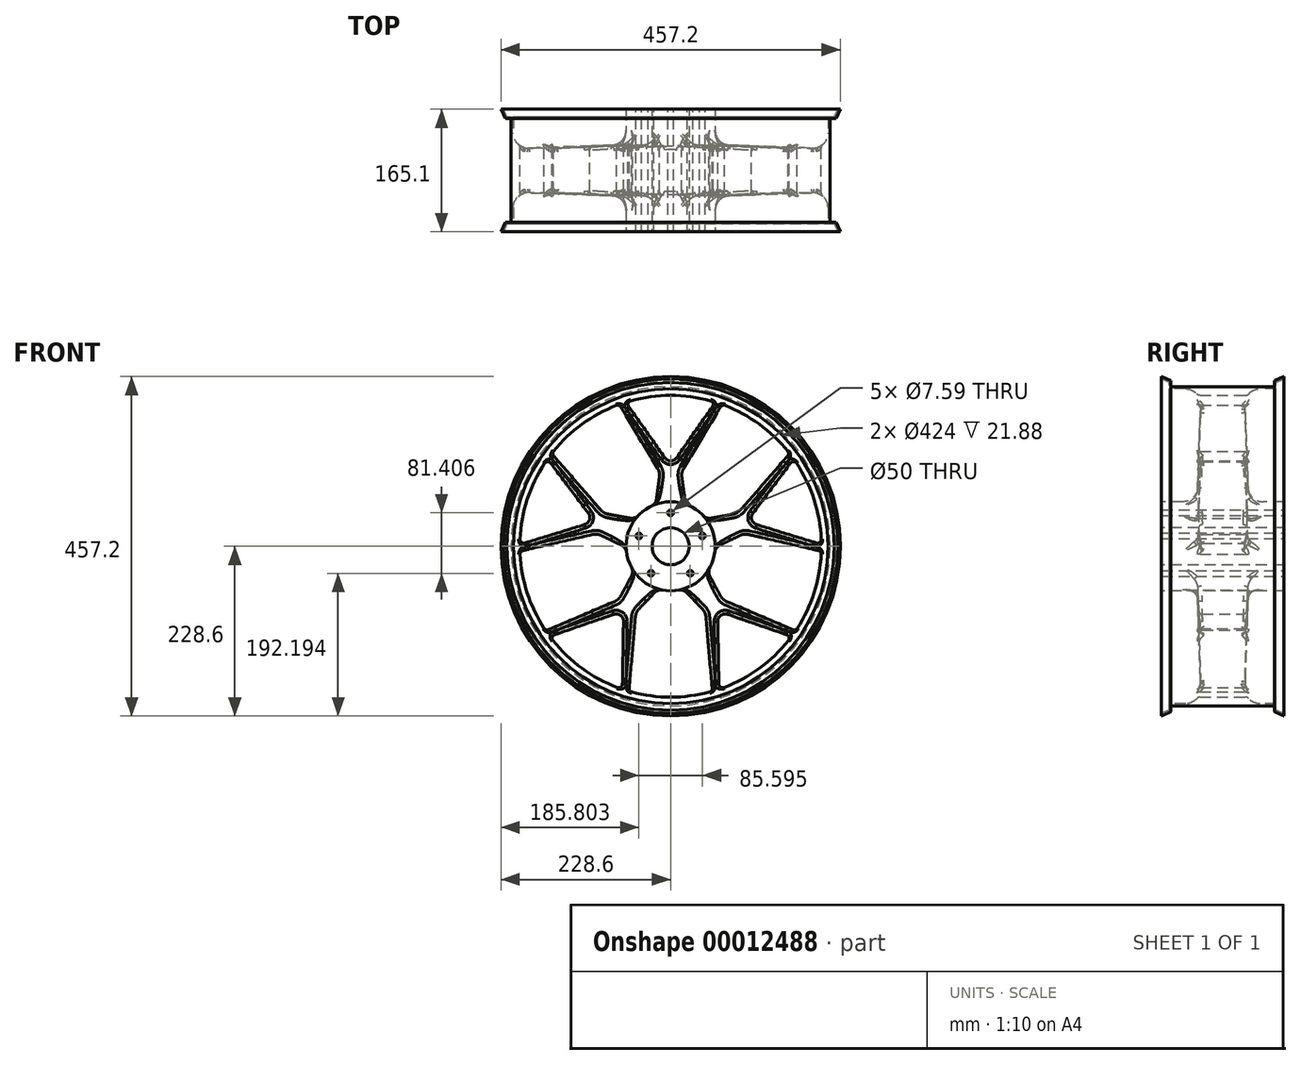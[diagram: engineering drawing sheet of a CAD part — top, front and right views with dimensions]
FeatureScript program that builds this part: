
annotation { "Feature Type Name" : "Feature", "Feature Type Description" : "" }
export const myFeature = defineFeature(function(context is Context, id is Id, definition is map)
    precondition{}
    {
        {
            var Q0;
            Q0=qCreatedBy(makeId("Right.planeOp"),FACE);
            var sketch = newSketch(context, id + "F0", { "sketchPlane" : qUnion([Q0])});
            skLineSegment(sketch, "E0", {"start": v(0, 0) * mm, "end": v(0, 215) * mm, "construction": true});
            skLineSegment(sketch, "E1", {"start": v(0, 215) * mm, "end": v(69.85, 215) * mm});
            skLineSegment(sketch, "E2", {"start": v(69.85, 215) * mm, "end": v(69.85, 223) * mm});
            skLineSegment(sketch, "E3", {"start": v(69.85, 223) * mm, "end": v(82.55, 228.6) * mm});
            skLineSegment(sketch, "E4", {"start": v(82.55, 228.6) * mm, "end": v(82.55, 225.32) * mm});
            skLineSegment(sketch, "E5", {"start": v(82.55, 225.32) * mm, "end": v(71.85, 220.6) * mm});
            skLineSegment(sketch, "E6", {"start": v(71.85, 220.6) * mm, "end": v(71.85, 212) * mm});
            skLineSegment(sketch, "E7", {"start": v(71.85, 212) * mm, "end": v(49.97, 212) * mm});
            skLineSegment(sketch, "E8", {"start": v(0, 0) * mm, "end": v(213.47, 0) * mm, "construction": true});
            skLineSegment(sketch, "E9", {"start": v(53.9, 60) * mm, "end": v(82.55, 60) * mm});
            skLineSegment(sketch, "E10", {"start": v(82.55, 60) * mm, "end": v(82.55, 25) * mm});
            skLineSegment(sketch, "E11", {"start": v(82.55, 25) * mm, "end": v(0, 25) * mm});
            skArc(sketch, "E12.filletArc", {"start": v(49.97, 212) * mm, "mid": v(35.6, 205.9) * mm, "end": v(30, 191.32) * mm});
            skLineSegment(sketch, "E13", {"start": v(30, 191.32) * mm, "end": v(33.91, 79.3) * mm});
            skPoint(sketch, "E14.newPointB", {"position": v(0, 60) * mm});
            skPoint(sketch, "E15.visualSharp", {"position": v(34.59, 60) * mm});
            skArc(sketch, "E15.filletArc", {"start": v(33.91, 79.3) * mm, "mid": v(40, 65.61) * mm, "end": v(53.9, 60) * mm});
            skLineSegment(sketch, "E16.0.MirrorCS", {"start": v(-69.85, 215) * mm, "end": v(-69.85, 223) * mm});
            skLineSegment(sketch, "E16.1.MirrorCS", {"start": v(-82.55, 228.6) * mm, "end": v(-82.55, 225.32) * mm});
            skLineSegment(sketch, "E16.2.MirrorCS", {"start": v(-71.85, 220.6) * mm, "end": v(-71.85, 212) * mm});
            skLineSegment(sketch, "E16.3.MirrorCS", {"start": v(-82.55, 225.32) * mm, "end": v(-71.85, 220.6) * mm});
            skLineSegment(sketch, "E16.4.MirrorCS", {"start": v(-82.55, 25) * mm, "end": v(0, 25) * mm});
            skArc(sketch, "E16.5.MirrorCS", {"start": v(-49.97, 212) * mm, "mid": v(-35.6, 205.9) * mm, "end": v(-30, 191.32) * mm});
            skLineSegment(sketch, "E16.6.MirrorCS", {"start": v(-53.9, 60) * mm, "end": v(-82.55, 60) * mm});
            skPoint(sketch, "E16.7.MirrorP", {"position": v(-34.59, 60) * mm});
            skLineSegment(sketch, "E16.8.MirrorCS", {"start": v(-69.85, 223) * mm, "end": v(-82.55, 228.6) * mm});
            skLineSegment(sketch, "E16.9.MirrorCS", {"start": v(-82.55, 60) * mm, "end": v(-82.55, 25) * mm});
            skLineSegment(sketch, "E16.10.MirrorCS", {"start": v(-71.85, 212) * mm, "end": v(-49.97, 212) * mm});
            skLineSegment(sketch, "E16.11.MirrorCS", {"start": v(0, 215) * mm, "end": v(-69.85, 215) * mm});
            skLineSegment(sketch, "E16.12.MirrorCS", {"start": v(-30, 191.32) * mm, "end": v(-33.91, 79.3) * mm});
            skArc(sketch, "E16.13.MirrorCS", {"start": v(-33.91, 79.3) * mm, "mid": v(-40, 65.61) * mm, "end": v(-53.9, 60) * mm});
            skSolve(sketch);
        }
        {
            var Q0;
            Q0 = qSketchRegion(id + "F0", true);
            var Q1;
            Q1=sQuery(id+"F0.wireOp",EDGE,"E8");
            revolve(context, id + "F1", {"entities" : qUnion([Q0]), "axis" : qUnion([Q1]), "revolveType" : RevolveType.FULL});
        }
        {
            var Q0;
            Q0=qCreatedBy(makeId("Front.planeOp"),FACE);
            var sketch = newSketch(context, id + "F2", { "sketchPlane" : qUnion([Q0])});
            skArc(sketch, "E17.0.MirrorCS", {"start": v(-19.12, 63.6) * mm, "mid": v(-21.4, 57.95) * mm, "end": v(-26.06, 54.04) * mm});
            skArc(sketch, "E17.1.MirrorCS", {"start": v(-17.45, 104.92) * mm, "mid": v(-15.27, 99.34) * mm, "end": v(-15.07, 93.35) * mm});
            skArc(sketch, "E17.2.MirrorCS", {"start": v(-72.74, 189.74) * mm, "mid": v(-69.52, 189.58) * mm, "end": v(-67.07, 187.5) * mm});
            skArc(sketch, "E17.3.MirrorCS", {"start": v(0, 115) * mm, "mid": v(-4.62, 116.13) * mm, "end": v(-8.2, 119.26) * mm});
            skLineSegment(sketch, "E17.5.MirrorCS", {"start": v(-19.12, 63.6) * mm, "end": v(-15.07, 93.35) * mm});
            skLineSegment(sketch, "E17.6.MirrorCS", {"start": v(-56.51, 188.28) * mm, "end": v(-8.2, 119.26) * mm});
            skLineSegment(sketch, "E17.7.MirrorCS", {"start": v(-17.45, 104.92) * mm, "end": v(-67.07, 187.5) * mm});
            skArc(sketch, "E17.8.MirrorCS", {"start": v(-56.51, 188.28) * mm, "mid": v(-57.12, 192.84) * mm, "end": v(-53.74, 195.96) * mm});
            skCircle(sketch, "E18", {"center": v(0, 45) * mm, "radius": 3.8 * mm});
            skLineSegment(sketch, "E19", {"start": v(0, 0) * mm, "end": v(-161.33, 222.05) * mm, "construction": true});
            skLineSegment(sketch, "E20", {"start": v(0, 0) * mm, "end": v(0, 224.28) * mm, "construction": true});
            skArc(sketch, "E21", {"start": v(0, 203.2) * mm, "mid": v(-27.11, 201.38) * mm, "end": v(-53.74, 195.96) * mm});
            skArc(sketch, "E22.trimOffspring", {"start": v(-72.74, 189.74) * mm, "mid": v(-96.92, 178.6) * mm, "end": v(-119.44, 164.4) * mm});
            skArc(sketch, "E23", {"start": v(-26.06, 54.04) * mm, "mid": v(-30.79, 51.5) * mm, "end": v(-35.27, 48.54) * mm});
            skArc(sketch, "E24.0.MirrorCS", {"start": v(0, 203.2) * mm, "mid": v(27.11, 201.38) * mm, "end": v(53.74, 195.96) * mm});
            skArc(sketch, "E25.0.MirrorCS", {"start": v(56.51, 188.28) * mm, "mid": v(57.12, 192.84) * mm, "end": v(53.74, 195.96) * mm});
            skLineSegment(sketch, "E26.0.MirrorCS", {"start": v(56.51, 188.28) * mm, "end": v(8.2, 119.26) * mm});
            skArc(sketch, "E27.0.MirrorCS", {"start": v(0, 115) * mm, "mid": v(4.62, 116.13) * mm, "end": v(8.2, 119.26) * mm});
            skArc(sketch, "E28.0.MirrorCS", {"start": v(-157.97, 127.8) * mm, "mid": v(-139.9, 147.37) * mm, "end": v(-119.44, 164.4) * mm});
            skArc(sketch, "E29.0.MirrorCS", {"start": v(-157.97, 127.8) * mm, "mid": v(-158.82, 124.7) * mm, "end": v(-157.6, 121.73) * mm});
            skLineSegment(sketch, "E30.0.MirrorCS", {"start": v(-94.4, 49.01) * mm, "end": v(-157.6, 121.73) * mm});
            skArc(sketch, "E31.0.MirrorCS", {"start": v(-94.4, 49.01) * mm, "mid": v(-89.75, 45.22) * mm, "end": v(-84.12, 43.17) * mm});
            skLineSegment(sketch, "E32.0.MirrorCS", {"start": v(-54.57, 37.84) * mm, "end": v(-84.12, 43.17) * mm});
            skArc(sketch, "E33.0.MirrorCS", {"start": v(-54.57, 37.84) * mm, "mid": v(-48.5, 38.25) * mm, "end": v(-43.34, 41.49) * mm});
            skArc(sketch, "E34.0.MirrorCS", {"start": v(-43.34, 41.49) * mm, "mid": v(-39.46, 45.2) * mm, "end": v(-35.27, 48.54) * mm});
            skArc(sketch, "E35.1.0", {"start": v(-170.37, -110.75) * mm, "mid": v(-183.39, -87.52) * mm, "end": v(-193.25, -62.8) * mm});
            skArc(sketch, "E35.1.1", {"start": v(-193.25, 62.8) * mm, "mid": v(-199.9, 36.45) * mm, "end": v(-202.98, 9.45) * mm});
            skLineSegment(sketch, "E35.1.2", {"start": v(-75.78, -74.63) * mm, "end": v(-164.47, -112.27) * mm});
            skArc(sketch, "E35.1.3", {"start": v(-202.93, -10.55) * mm, "mid": v(-199.8, -36.99) * mm, "end": v(-193.25, -62.8) * mm});
            skArc(sketch, "E35.1.4", {"start": v(-170.37, -110.75) * mm, "mid": v(-167.68, -112.51) * mm, "end": v(-164.47, -112.27) * mm});
            skLineSegment(sketch, "E35.1.5", {"start": v(-161.6, 111.93) * mm, "end": v(-110.9, 44.65) * mm});
            skLineSegment(sketch, "E35.1.6", {"start": v(-52.85, -40.21) * mm, "end": v(-67.06, -66.66) * mm});
            skArc(sketch, "E35.1.7", {"start": v(-109.37, 35.54) * mm, "mid": v(-111.87, 31.5) * mm, "end": v(-115.96, 29.06) * mm});
            skLineSegment(sketch, "E35.1.8", {"start": v(-66.4, 1.47) * mm, "end": v(-93.43, 14.52) * mm});
            skLineSegment(sketch, "E35.1.9", {"start": v(-196.52, 4.43) * mm, "end": v(-115.96, 29.06) * mm});
            skLineSegment(sketch, "E35.1.10", {"start": v(-105.17, 15.83) * mm, "end": v(-199.05, -5.84) * mm});
            skArc(sketch, "E35.1.11", {"start": v(-161.6, 111.93) * mm, "mid": v(-165.75, 113.92) * mm, "end": v(-169.77, 111.67) * mm});
            skArc(sketch, "E35.1.12", {"start": v(-193.25, 62.8) * mm, "mid": v(-183.15, 88.02) * mm, "end": v(-169.77, 111.67) * mm});
            skArc(sketch, "E35.1.13", {"start": v(-202.93, -10.55) * mm, "mid": v(-201.79, -7.54) * mm, "end": v(-199.05, -5.84) * mm});
            skArc(sketch, "E35.1.14", {"start": v(-109.37, 35.54) * mm, "mid": v(-109.02, 40.28) * mm, "end": v(-110.9, 44.65) * mm});
            skCircle(sketch, "E35.1.15", {"center": v(-42.8, 13.9) * mm, "radius": 3.8 * mm});
            skArc(sketch, "E35.1.16", {"start": v(-196.52, 4.43) * mm, "mid": v(-201.05, 5.27) * mm, "end": v(-202.98, 9.45) * mm});
            skArc(sketch, "E35.1.17", {"start": v(-75.78, -74.63) * mm, "mid": v(-70.74, -71.39) * mm, "end": v(-67.06, -66.66) * mm});
            skArc(sketch, "E35.1.18", {"start": v(-59.45, -8.09) * mm, "mid": v(-58.5, -13.37) * mm, "end": v(-57.06, -18.54) * mm});
            skArc(sketch, "E35.1.19", {"start": v(-52.85, -28.4) * mm, "mid": v(-55.18, -23.57) * mm, "end": v(-57.06, -18.54) * mm});
            skArc(sketch, "E35.1.20", {"start": v(-66.4, 1.47) * mm, "mid": v(-61.72, -2.44) * mm, "end": v(-59.45, -8.09) * mm});
            skArc(sketch, "E35.1.21", {"start": v(-52.85, -40.21) * mm, "mid": v(-51.37, -34.3) * mm, "end": v(-52.85, -28.4) * mm});
            skArc(sketch, "E35.1.22", {"start": v(-105.17, 15.83) * mm, "mid": v(-99.2, 16.17) * mm, "end": v(-93.43, 14.52) * mm});
            skArc(sketch, "E35.2.0", {"start": v(52.68, -196.25) * mm, "mid": v(26.57, -201.46) * mm, "end": v(0, -203.2) * mm});
            skArc(sketch, "E35.2.1", {"start": v(-119.44, -164.4) * mm, "mid": v(-96.44, -178.86) * mm, "end": v(-71.7, -190.13) * mm});
            skLineSegment(sketch, "E35.2.2", {"start": v(47.55, -95.14) * mm, "end": v(55.95, -191.12) * mm});
            skArc(sketch, "E35.2.3", {"start": v(-52.68, -196.25) * mm, "mid": v(-26.57, -201.46) * mm, "end": v(0, -203.2) * mm});
            skArc(sketch, "E35.2.4", {"start": v(52.68, -196.25) * mm, "mid": v(55.19, -194.24) * mm, "end": v(55.95, -191.12) * mm});
            skLineSegment(sketch, "E35.2.5", {"start": v(-156.39, -119.1) * mm, "end": v(-76.73, -91.67) * mm});
            skLineSegment(sketch, "E35.2.6", {"start": v(21.91, -62.69) * mm, "end": v(42.68, -84.37) * mm});
            skArc(sketch, "E35.2.7", {"start": v(-67.6, -93.04) * mm, "mid": v(-64.52, -96.67) * mm, "end": v(-63.47, -101.3) * mm});
            skLineSegment(sketch, "E35.2.8", {"start": v(-21.91, -62.69) * mm, "end": v(-42.68, -84.37) * mm});
            skLineSegment(sketch, "E35.2.9", {"start": v(-64.94, -185.54) * mm, "end": v(-63.47, -101.3) * mm});
            skLineSegment(sketch, "E35.2.10", {"start": v(-47.55, -95.14) * mm, "end": v(-55.95, -191.12) * mm});
            skArc(sketch, "E35.2.11", {"start": v(-156.39, -119.1) * mm, "mid": v(-159.56, -122.44) * mm, "end": v(-158.66, -126.95) * mm});
            skArc(sketch, "E35.2.12", {"start": v(-119.44, -164.4) * mm, "mid": v(-140.3, -146.99) * mm, "end": v(-158.66, -126.95) * mm});
            skArc(sketch, "E35.2.13", {"start": v(-52.68, -196.25) * mm, "mid": v(-55.19, -194.24) * mm, "end": v(-55.95, -191.12) * mm});
            skArc(sketch, "E35.2.14", {"start": v(-67.6, -93.04) * mm, "mid": v(-72, -91.24) * mm, "end": v(-76.73, -91.67) * mm});
            skCircle(sketch, "E35.2.15", {"center": v(-26.45, -36.4) * mm, "radius": 3.8 * mm});
            skArc(sketch, "E35.2.16", {"start": v(-64.94, -185.54) * mm, "mid": v(-67.14, -189.59) * mm, "end": v(-71.7, -190.13) * mm});
            skArc(sketch, "E35.2.17", {"start": v(47.55, -95.14) * mm, "mid": v(46.04, -89.34) * mm, "end": v(42.68, -84.37) * mm});
            skArc(sketch, "E35.2.18", {"start": v(-10.68, -59.04) * mm, "mid": v(-5.36, -59.76) * mm, "end": v(0, -60) * mm});
            skArc(sketch, "E35.2.19", {"start": v(10.68, -59.04) * mm, "mid": v(5.36, -59.76) * mm, "end": v(0, -60) * mm});
            skArc(sketch, "E35.2.20", {"start": v(-21.91, -62.69) * mm, "mid": v(-16.76, -59.45) * mm, "end": v(-10.68, -59.04) * mm});
            skArc(sketch, "E35.2.21", {"start": v(21.91, -62.69) * mm, "mid": v(16.76, -59.45) * mm, "end": v(10.68, -59.04) * mm});
            skArc(sketch, "E35.2.22", {"start": v(-47.55, -95.14) * mm, "mid": v(-46.04, -89.34) * mm, "end": v(-42.68, -84.37) * mm});
            skArc(sketch, "E35.3.0", {"start": v(202.93, -10.55) * mm, "mid": v(199.8, -36.99) * mm, "end": v(193.25, -62.8) * mm});
            skArc(sketch, "E35.3.1", {"start": v(119.44, -164.4) * mm, "mid": v(140.3, -146.99) * mm, "end": v(158.66, -126.95) * mm});
            skLineSegment(sketch, "E35.3.2", {"start": v(105.17, 15.83) * mm, "end": v(199.05, -5.84) * mm});
            skArc(sketch, "E35.3.3", {"start": v(170.37, -110.75) * mm, "mid": v(183.39, -87.52) * mm, "end": v(193.25, -62.8) * mm});
            skArc(sketch, "E35.3.4", {"start": v(202.93, -10.55) * mm, "mid": v(201.79, -7.54) * mm, "end": v(199.05, -5.84) * mm});
            skLineSegment(sketch, "E35.3.5", {"start": v(64.94, -185.54) * mm, "end": v(63.47, -101.3) * mm});
            skLineSegment(sketch, "E35.3.6", {"start": v(66.4, 1.47) * mm, "end": v(93.43, 14.52) * mm});
            skArc(sketch, "E35.3.7", {"start": v(67.6, -93.04) * mm, "mid": v(72, -91.24) * mm, "end": v(76.73, -91.67) * mm});
            skLineSegment(sketch, "E35.3.8", {"start": v(52.85, -40.21) * mm, "end": v(67.06, -66.66) * mm});
            skLineSegment(sketch, "E35.3.9", {"start": v(156.39, -119.1) * mm, "end": v(76.73, -91.67) * mm});
            skLineSegment(sketch, "E35.3.10", {"start": v(75.78, -74.63) * mm, "end": v(164.47, -112.27) * mm});
            skArc(sketch, "E35.3.11", {"start": v(64.94, -185.54) * mm, "mid": v(67.14, -189.59) * mm, "end": v(71.7, -190.13) * mm});
            skArc(sketch, "E35.3.12", {"start": v(119.44, -164.4) * mm, "mid": v(96.44, -178.86) * mm, "end": v(71.7, -190.13) * mm});
            skArc(sketch, "E35.3.13", {"start": v(170.37, -110.75) * mm, "mid": v(167.68, -112.51) * mm, "end": v(164.47, -112.27) * mm});
            skArc(sketch, "E35.3.14", {"start": v(67.6, -93.04) * mm, "mid": v(64.52, -96.67) * mm, "end": v(63.47, -101.3) * mm});
            skCircle(sketch, "E35.3.15", {"center": v(26.45, -36.4) * mm, "radius": 3.8 * mm});
            skArc(sketch, "E35.3.16", {"start": v(156.39, -119.1) * mm, "mid": v(159.56, -122.44) * mm, "end": v(158.66, -126.95) * mm});
            skArc(sketch, "E35.3.17", {"start": v(105.17, 15.83) * mm, "mid": v(99.2, 16.17) * mm, "end": v(93.43, 14.52) * mm});
            skArc(sketch, "E35.3.18", {"start": v(52.85, -28.4) * mm, "mid": v(55.18, -23.57) * mm, "end": v(57.06, -18.54) * mm});
            skArc(sketch, "E35.3.19", {"start": v(59.45, -8.09) * mm, "mid": v(58.5, -13.37) * mm, "end": v(57.06, -18.54) * mm});
            skArc(sketch, "E35.3.20", {"start": v(52.85, -40.21) * mm, "mid": v(51.37, -34.3) * mm, "end": v(52.85, -28.4) * mm});
            skArc(sketch, "E35.3.21", {"start": v(66.4, 1.47) * mm, "mid": v(61.72, -2.44) * mm, "end": v(59.45, -8.09) * mm});
            skArc(sketch, "E35.3.22", {"start": v(75.78, -74.63) * mm, "mid": v(70.74, -71.39) * mm, "end": v(67.06, -66.66) * mm});
            skArc(sketch, "E35.4.0", {"start": v(72.74, 189.74) * mm, "mid": v(96.92, 178.6) * mm, "end": v(119.44, 164.4) * mm});
            skArc(sketch, "E35.4.1", {"start": v(193.25, 62.8) * mm, "mid": v(183.15, 88.02) * mm, "end": v(169.77, 111.67) * mm});
            skLineSegment(sketch, "E35.4.2", {"start": v(17.45, 104.92) * mm, "end": v(67.07, 187.5) * mm});
            skArc(sketch, "E35.4.3", {"start": v(157.97, 127.8) * mm, "mid": v(139.9, 147.37) * mm, "end": v(119.44, 164.4) * mm});
            skArc(sketch, "E35.4.4", {"start": v(72.74, 189.74) * mm, "mid": v(69.52, 189.58) * mm, "end": v(67.07, 187.5) * mm});
            skLineSegment(sketch, "E35.4.5", {"start": v(196.52, 4.43) * mm, "end": v(115.96, 29.06) * mm});
            skLineSegment(sketch, "E35.4.6", {"start": v(19.12, 63.6) * mm, "end": v(15.07, 93.35) * mm});
            skArc(sketch, "E35.4.7", {"start": v(109.37, 35.54) * mm, "mid": v(109.02, 40.28) * mm, "end": v(110.9, 44.65) * mm});
            skLineSegment(sketch, "E35.4.8", {"start": v(54.57, 37.84) * mm, "end": v(84.12, 43.17) * mm});
            skLineSegment(sketch, "E35.4.9", {"start": v(161.6, 111.93) * mm, "end": v(110.9, 44.65) * mm});
            skLineSegment(sketch, "E35.4.10", {"start": v(94.4, 49.01) * mm, "end": v(157.6, 121.73) * mm});
            skArc(sketch, "E35.4.11", {"start": v(196.52, 4.43) * mm, "mid": v(201.05, 5.27) * mm, "end": v(202.98, 9.45) * mm});
            skArc(sketch, "E35.4.12", {"start": v(193.25, 62.8) * mm, "mid": v(199.9, 36.45) * mm, "end": v(202.98, 9.45) * mm});
            skArc(sketch, "E35.4.13", {"start": v(157.97, 127.8) * mm, "mid": v(158.82, 124.7) * mm, "end": v(157.6, 121.73) * mm});
            skArc(sketch, "E35.4.14", {"start": v(109.37, 35.54) * mm, "mid": v(111.87, 31.5) * mm, "end": v(115.96, 29.06) * mm});
            skCircle(sketch, "E35.4.15", {"center": v(42.8, 13.9) * mm, "radius": 3.8 * mm});
            skArc(sketch, "E35.4.16", {"start": v(161.6, 111.93) * mm, "mid": v(165.75, 113.92) * mm, "end": v(169.77, 111.67) * mm});
            skArc(sketch, "E35.4.17", {"start": v(17.45, 104.92) * mm, "mid": v(15.27, 99.34) * mm, "end": v(15.07, 93.35) * mm});
            skArc(sketch, "E35.4.18", {"start": v(43.34, 41.49) * mm, "mid": v(39.46, 45.2) * mm, "end": v(35.27, 48.54) * mm});
            skArc(sketch, "E35.4.19", {"start": v(26.06, 54.04) * mm, "mid": v(30.79, 51.5) * mm, "end": v(35.27, 48.54) * mm});
            skArc(sketch, "E35.4.20", {"start": v(54.57, 37.84) * mm, "mid": v(48.5, 38.25) * mm, "end": v(43.34, 41.49) * mm});
            skArc(sketch, "E35.4.21", {"start": v(19.12, 63.6) * mm, "mid": v(21.4, 57.95) * mm, "end": v(26.06, 54.04) * mm});
            skArc(sketch, "E35.4.22", {"start": v(94.4, 49.01) * mm, "mid": v(89.75, 45.22) * mm, "end": v(84.12, 43.17) * mm});
            skSolve(sketch);
        }
        {
            var Q0;
            Q0 = qSketchRegion(id + "F2", true);
            extrude(context, id + "F3", {"entities" : qUnion([Q0]), "operationType" : NewBodyOperationType.REMOVE, "endBound" : BoundingType.THROUGH_ALL, "depth" : 25 * mm, "hasSecondDirection" : true, "secondDirectionBound" : SecondDirectionBoundingType.THROUGH_ALL, "secondDirectionOppositeDirection" : true, "secondDirectionDepth" : 25 * mm});
        }
        {
            var Q0;
            Q0=makeQuery(id+"F3.boolean.opBoolean","INTERSECT",EDGE,{"derivedFrom":[makeQuery(id+"F1.opRevolve","SWEPT_FACE",FACE,{"disambiguationData":[OSD([sQuery(id+"F0.wireOp",EDGE,"E13")])]}),makeQuery(id+"F3.opExtrude","SWEPT_FACE",FACE,{"disambiguationData":[OSD([sQuery(id+"F2.wireOp",EDGE,"E26.0.MirrorCS")])]})]});
            var Q1;
            Q1=makeQuery(id+"F3.boolean.opBoolean","INTERSECT",EDGE,{"derivedFrom":[makeQuery(id+"F1.opRevolve","SWEPT_FACE",FACE,{"disambiguationData":[OSD([sQuery(id+"F0.wireOp",EDGE,"E13")])]}),makeQuery(id+"F3.opExtrude","SWEPT_FACE",FACE,{"disambiguationData":[OSD([sQuery(id+"F2.wireOp",EDGE,"E17.7.MirrorCS")])]})]});
            var Q2;
            Q2=makeQuery(id+"F3.boolean.opBoolean","INTERSECT",EDGE,{"derivedFrom":[makeQuery(id+"F1.opRevolve","SWEPT_FACE",FACE,{"disambiguationData":[OSD([sQuery(id+"F0.wireOp",EDGE,"E13")])]}),makeQuery(id+"F3.opExtrude","SWEPT_FACE",FACE,{"disambiguationData":[OSD([sQuery(id+"F2.wireOp",EDGE,"E35.1.5")])]})]});
            var Q3;
            Q3=makeQuery(id+"F3.boolean.opBoolean","INTERSECT",EDGE,{"derivedFrom":[makeQuery(id+"F1.opRevolve","SWEPT_FACE",FACE,{"disambiguationData":[OSD([sQuery(id+"F0.wireOp",EDGE,"E13")])]}),makeQuery(id+"F3.opExtrude","SWEPT_FACE",FACE,{"disambiguationData":[OSD([sQuery(id+"F2.wireOp",EDGE,"E35.1.10")])]})]});
            var Q4;
            Q4=makeQuery(id+"F3.boolean.opBoolean","INTERSECT",EDGE,{"derivedFrom":[makeQuery(id+"F1.opRevolve","SWEPT_FACE",FACE,{"disambiguationData":[OSD([sQuery(id+"F0.wireOp",EDGE,"E13")])]}),makeQuery(id+"F3.opExtrude","SWEPT_FACE",FACE,{"disambiguationData":[OSD([sQuery(id+"F2.wireOp",EDGE,"E35.2.5")])]})]});
            var Q5;
            Q5=makeQuery(id+"F3.boolean.opBoolean","INTERSECT",EDGE,{"derivedFrom":[makeQuery(id+"F1.opRevolve","SWEPT_FACE",FACE,{"disambiguationData":[OSD([sQuery(id+"F0.wireOp",EDGE,"E13")])]}),makeQuery(id+"F3.opExtrude","SWEPT_FACE",FACE,{"disambiguationData":[OSD([sQuery(id+"F2.wireOp",EDGE,"E35.2.10")])]})]});
            var Q6;
            Q6=makeQuery(id+"F3.boolean.opBoolean","INTERSECT",EDGE,{"derivedFrom":[makeQuery(id+"F1.opRevolve","SWEPT_FACE",FACE,{"disambiguationData":[OSD([sQuery(id+"F0.wireOp",EDGE,"E13")])]}),makeQuery(id+"F3.opExtrude","SWEPT_FACE",FACE,{"disambiguationData":[OSD([sQuery(id+"F2.wireOp",EDGE,"E35.3.5")])]})]});
            var Q7;
            Q7=makeQuery(id+"F3.boolean.opBoolean","INTERSECT",EDGE,{"derivedFrom":[makeQuery(id+"F1.opRevolve","SWEPT_FACE",FACE,{"disambiguationData":[OSD([sQuery(id+"F0.wireOp",EDGE,"E13")])]}),makeQuery(id+"F3.opExtrude","SWEPT_FACE",FACE,{"disambiguationData":[OSD([sQuery(id+"F2.wireOp",EDGE,"E35.3.10")])]})]});
            var Q8;
            Q8=makeQuery(id+"F3.boolean.opBoolean","INTERSECT",EDGE,{"derivedFrom":[makeQuery(id+"F1.opRevolve","SWEPT_FACE",FACE,{"disambiguationData":[OSD([sQuery(id+"F0.wireOp",EDGE,"E13")])]}),makeQuery(id+"F3.opExtrude","SWEPT_FACE",FACE,{"disambiguationData":[OSD([sQuery(id+"F2.wireOp",EDGE,"E35.4.5")])]})]});
            var Q9;
            Q9=makeQuery(id+"F3.boolean.opBoolean","INTERSECT",EDGE,{"derivedFrom":[makeQuery(id+"F1.opRevolve","SWEPT_FACE",FACE,{"disambiguationData":[OSD([sQuery(id+"F0.wireOp",EDGE,"E13")])]}),makeQuery(id+"F3.opExtrude","SWEPT_FACE",FACE,{"disambiguationData":[OSD([sQuery(id+"F2.wireOp",EDGE,"E35.4.10")])]})]});
            var Q10;
            Q10=makeQuery(id+"F3.boolean.opBoolean","INTERSECT",EDGE,{"derivedFrom":[makeQuery(id+"F1.opRevolve","SWEPT_FACE",FACE,{"disambiguationData":[OSD([sQuery(id+"F0.wireOp",EDGE,"E16.12.MirrorCS")])]}),makeQuery(id+"F3.opExtrude","SWEPT_FACE",FACE,{"disambiguationData":[OSD([sQuery(id+"F2.wireOp",EDGE,"E35.4.10")])]})]});
            var Q11;
            Q11=makeQuery(id+"F3.boolean.opBoolean","INTERSECT",EDGE,{"derivedFrom":[makeQuery(id+"F1.opRevolve","SWEPT_FACE",FACE,{"disambiguationData":[OSD([sQuery(id+"F0.wireOp",EDGE,"E16.12.MirrorCS")])]}),makeQuery(id+"F3.opExtrude","SWEPT_FACE",FACE,{"disambiguationData":[OSD([sQuery(id+"F2.wireOp",EDGE,"E35.4.9")])]})]});
            var Q12;
            Q12=makeQuery(id+"F3.boolean.opBoolean","INTERSECT",EDGE,{"derivedFrom":[makeQuery(id+"F1.opRevolve","SWEPT_FACE",FACE,{"disambiguationData":[OSD([sQuery(id+"F0.wireOp",EDGE,"E16.12.MirrorCS")])]}),makeQuery(id+"F3.opExtrude","SWEPT_FACE",FACE,{"disambiguationData":[OSD([sQuery(id+"F2.wireOp",EDGE,"E35.3.2")])]})]});
            var Q13;
            Q13=makeQuery(id+"F3.boolean.opBoolean","INTERSECT",EDGE,{"derivedFrom":[makeQuery(id+"F1.opRevolve","SWEPT_FACE",FACE,{"disambiguationData":[OSD([sQuery(id+"F0.wireOp",EDGE,"E16.12.MirrorCS")])]}),makeQuery(id+"F3.opExtrude","SWEPT_FACE",FACE,{"disambiguationData":[OSD([sQuery(id+"F2.wireOp",EDGE,"E35.3.9")])]})]});
            var Q14;
            Q14=makeQuery(id+"F3.boolean.opBoolean","INTERSECT",EDGE,{"derivedFrom":[makeQuery(id+"F1.opRevolve","SWEPT_FACE",FACE,{"disambiguationData":[OSD([sQuery(id+"F0.wireOp",EDGE,"E16.12.MirrorCS")])]}),makeQuery(id+"F3.opExtrude","SWEPT_FACE",FACE,{"disambiguationData":[OSD([sQuery(id+"F2.wireOp",EDGE,"E35.2.2")])]})]});
            var Q15;
            Q15=makeQuery(id+"F3.boolean.opBoolean","INTERSECT",EDGE,{"derivedFrom":[makeQuery(id+"F1.opRevolve","SWEPT_FACE",FACE,{"disambiguationData":[OSD([sQuery(id+"F0.wireOp",EDGE,"E16.12.MirrorCS")])]}),makeQuery(id+"F3.opExtrude","SWEPT_FACE",FACE,{"disambiguationData":[OSD([sQuery(id+"F2.wireOp",EDGE,"E35.2.9")])]})]});
            var Q16;
            Q16=makeQuery(id+"F3.boolean.opBoolean","INTERSECT",EDGE,{"derivedFrom":[makeQuery(id+"F1.opRevolve","SWEPT_FACE",FACE,{"disambiguationData":[OSD([sQuery(id+"F0.wireOp",EDGE,"E16.12.MirrorCS")])]}),makeQuery(id+"F3.opExtrude","SWEPT_FACE",FACE,{"disambiguationData":[OSD([sQuery(id+"F2.wireOp",EDGE,"E35.1.2")])]})]});
            var Q17;
            Q17=makeQuery(id+"F3.boolean.opBoolean","INTERSECT",EDGE,{"derivedFrom":[makeQuery(id+"F1.opRevolve","SWEPT_FACE",FACE,{"disambiguationData":[OSD([sQuery(id+"F0.wireOp",EDGE,"E16.12.MirrorCS")])]}),makeQuery(id+"F3.opExtrude","SWEPT_FACE",FACE,{"disambiguationData":[OSD([sQuery(id+"F2.wireOp",EDGE,"E35.1.9")])]})]});
            var Q18;
            Q18=makeQuery(id+"F3.boolean.opBoolean","INTERSECT",EDGE,{"derivedFrom":[makeQuery(id+"F1.opRevolve","SWEPT_FACE",FACE,{"disambiguationData":[OSD([sQuery(id+"F0.wireOp",EDGE,"E16.12.MirrorCS")])]}),makeQuery(id+"F3.opExtrude","SWEPT_FACE",FACE,{"disambiguationData":[OSD([sQuery(id+"F2.wireOp",EDGE,"E30.0.MirrorCS")])]})]});
            var Q19;
            Q19=makeQuery(id+"F3.boolean.opBoolean","INTERSECT",EDGE,{"derivedFrom":[makeQuery(id+"F1.opRevolve","SWEPT_FACE",FACE,{"disambiguationData":[OSD([sQuery(id+"F0.wireOp",EDGE,"E16.12.MirrorCS")])]}),makeQuery(id+"F3.opExtrude","SWEPT_FACE",FACE,{"disambiguationData":[OSD([sQuery(id+"F2.wireOp",EDGE,"E26.0.MirrorCS")])]})]});
            var Q20;
            Q20=makeQuery(id+"F3.boolean.opBoolean","INTERSECT",EDGE,{"derivedFrom":[makeQuery(id+"F1.opRevolve","SWEPT_FACE",FACE,{"disambiguationData":[OSD([sQuery(id+"F0.wireOp",EDGE,"E13")])]}),makeQuery(id+"F3.opExtrude","SWEPT_FACE",FACE,{"disambiguationData":[OSD([sQuery(id+"F2.wireOp",EDGE,"E35.4.17")])]})]});
            var Q21;
            Q21=makeQuery(id+"F3.boolean.opBoolean","INTERSECT",EDGE,{"derivedFrom":[makeQuery(id+"F1.opRevolve","SWEPT_FACE",FACE,{"disambiguationData":[OSD([sQuery(id+"F0.wireOp",EDGE,"E13")])]}),makeQuery(id+"F3.opExtrude","SWEPT_FACE",FACE,{"disambiguationData":[OSD([sQuery(id+"F2.wireOp",EDGE,"E35.3.2")])]})]});
            var Q22;
            Q22=makeQuery(id+"F3.boolean.opBoolean","INTERSECT",EDGE,{"derivedFrom":[makeQuery(id+"F1.opRevolve","SWEPT_FACE",FACE,{"disambiguationData":[OSD([sQuery(id+"F0.wireOp",EDGE,"E13")])]}),makeQuery(id+"F3.opExtrude","SWEPT_FACE",FACE,{"disambiguationData":[OSD([sQuery(id+"F2.wireOp",EDGE,"E35.2.6")])]})]});
            var Q23;
            Q23=makeQuery(id+"F3.boolean.opBoolean","INTERSECT",EDGE,{"derivedFrom":[makeQuery(id+"F1.opRevolve","SWEPT_FACE",FACE,{"disambiguationData":[OSD([sQuery(id+"F0.wireOp",EDGE,"E16.12.MirrorCS")])]}),makeQuery(id+"F3.opExtrude","SWEPT_FACE",FACE,{"disambiguationData":[OSD([sQuery(id+"F2.wireOp",EDGE,"E35.3.10")])]})]});
            var Q24;
            Q24=makeQuery(id+"F3.boolean.opBoolean","INTERSECT",EDGE,{"derivedFrom":[makeQuery(id+"F1.opRevolve","SWEPT_FACE",FACE,{"disambiguationData":[OSD([sQuery(id+"F0.wireOp",EDGE,"E16.12.MirrorCS")])]}),makeQuery(id+"F3.opExtrude","SWEPT_FACE",FACE,{"disambiguationData":[OSD([sQuery(id+"F2.wireOp",EDGE,"E17.5.MirrorCS")])]})]});
            var Q25;
            Q25=makeQuery(id+"F3.boolean.opBoolean","INTERSECT",EDGE,{"derivedFrom":[makeQuery(id+"F1.opRevolve","SWEPT_FACE",FACE,{"disambiguationData":[OSD([sQuery(id+"F0.wireOp",EDGE,"E16.12.MirrorCS")])]}),makeQuery(id+"F3.opExtrude","SWEPT_FACE",FACE,{"disambiguationData":[OSD([sQuery(id+"F2.wireOp",EDGE,"E35.4.17")])]})]});
            var Q26;
            Q26=makeQuery(id+"F3.boolean.opBoolean","INTERSECT",EDGE,{"derivedFrom":[makeQuery(id+"F1.opRevolve","SWEPT_FACE",FACE,{"disambiguationData":[OSD([sQuery(id+"F0.wireOp",EDGE,"E16.12.MirrorCS")])]}),makeQuery(id+"F3.opExtrude","SWEPT_FACE",FACE,{"disambiguationData":[OSD([sQuery(id+"F2.wireOp",EDGE,"E35.1.8")])]})]});
            var Q27;
            Q27=makeQuery(id+"F3.boolean.opBoolean","INTERSECT",EDGE,{"derivedFrom":[makeQuery(id+"F1.opRevolve","SWEPT_FACE",FACE,{"disambiguationData":[OSD([sQuery(id+"F0.wireOp",EDGE,"E16.12.MirrorCS")])]}),makeQuery(id+"F3.opExtrude","SWEPT_FACE",FACE,{"disambiguationData":[OSD([sQuery(id+"F2.wireOp",EDGE,"E35.2.8")])]})]});
            var Q28;
            Q28=makeQuery(id+"F3.boolean.opBoolean","INTERSECT",EDGE,{"derivedFrom":[makeQuery(id+"F1.opRevolve","SWEPT_FACE",FACE,{"disambiguationData":[OSD([sQuery(id+"F0.wireOp",EDGE,"E13")])]}),makeQuery(id+"F3.opExtrude","SWEPT_FACE",FACE,{"disambiguationData":[OSD([sQuery(id+"F2.wireOp",EDGE,"E30.0.MirrorCS")])]})]});
            var Q29;
            Q29=makeQuery(id+"F3.boolean.opBoolean","INTERSECT",EDGE,{"derivedFrom":[makeQuery(id+"F1.opRevolve","SWEPT_FACE",FACE,{"disambiguationData":[OSD([sQuery(id+"F0.wireOp",EDGE,"E13")])]}),makeQuery(id+"F3.opExtrude","SWEPT_FACE",FACE,{"disambiguationData":[OSD([sQuery(id+"F2.wireOp",EDGE,"E35.1.2")])]})]});
            var Q30;
            Q30=makeQuery(id+"F3.boolean.opBoolean","INTERSECT",EDGE,{"derivedFrom":[makeQuery(id+"F1.opRevolve","SWEPT_FACE",FACE,{"disambiguationData":[OSD([sQuery(id+"F0.wireOp",EDGE,"E16.5.MirrorCS")])]}),makeQuery(id+"F3.opExtrude","SWEPT_FACE",FACE,{"disambiguationData":[OSD([sQuery(id+"F2.wireOp",EDGE,"E35.1.0"),sQuery(id+"F2.wireOp",EDGE,"E35.1.3")])]})]});
            var Q31;
            Q31=makeQuery(id+"F3.boolean.opBoolean","INTERSECT",EDGE,{"derivedFrom":[makeQuery(id+"F1.opRevolve","SWEPT_FACE",FACE,{"disambiguationData":[OSD([sQuery(id+"F0.wireOp",EDGE,"E16.5.MirrorCS")])]}),makeQuery(id+"F3.opExtrude","SWEPT_FACE",FACE,{"disambiguationData":[OSD([sQuery(id+"F2.wireOp",EDGE,"E22.trimOffspring"),sQuery(id+"F2.wireOp",EDGE,"E28.0.MirrorCS")])]})]});
            var Q32;
            Q32=makeQuery(id+"F3.boolean.opBoolean","INTERSECT",EDGE,{"derivedFrom":[makeQuery(id+"F1.opRevolve","SWEPT_FACE",FACE,{"disambiguationData":[OSD([sQuery(id+"F0.wireOp",EDGE,"E16.5.MirrorCS")])]}),makeQuery(id+"F3.opExtrude","SWEPT_FACE",FACE,{"disambiguationData":[OSD([sQuery(id+"F2.wireOp",EDGE,"E35.4.0"),sQuery(id+"F2.wireOp",EDGE,"E35.4.3")])]})]});
            var Q33;
            Q33=makeQuery(id+"F3.boolean.opBoolean","INTERSECT",EDGE,{"derivedFrom":[makeQuery(id+"F1.opRevolve","SWEPT_FACE",FACE,{"disambiguationData":[OSD([sQuery(id+"F0.wireOp",EDGE,"E16.5.MirrorCS")])]}),makeQuery(id+"F3.opExtrude","SWEPT_FACE",FACE,{"disambiguationData":[OSD([sQuery(id+"F2.wireOp",EDGE,"E35.3.0"),sQuery(id+"F2.wireOp",EDGE,"E35.3.3")])]})]});
            var Q34;
            Q34=makeQuery(id+"F3.boolean.opBoolean","INTERSECT",EDGE,{"derivedFrom":[makeQuery(id+"F1.opRevolve","SWEPT_FACE",FACE,{"disambiguationData":[OSD([sQuery(id+"F0.wireOp",EDGE,"E16.5.MirrorCS")])]}),makeQuery(id+"F3.opExtrude","SWEPT_FACE",FACE,{"disambiguationData":[OSD([sQuery(id+"F2.wireOp",EDGE,"E35.2.0"),sQuery(id+"F2.wireOp",EDGE,"E35.2.3")])]})]});
            var Q35;
            Q35=makeQuery(id+"F3.boolean.opBoolean","INTERSECT",EDGE,{"derivedFrom":[makeQuery(id+"F1.opRevolve","SWEPT_FACE",FACE,{"disambiguationData":[OSD([sQuery(id+"F0.wireOp",EDGE,"E12.filletArc")])]}),makeQuery(id+"F3.opExtrude","SWEPT_FACE",FACE,{"disambiguationData":[OSD([sQuery(id+"F2.wireOp",EDGE,"E35.2.0"),sQuery(id+"F2.wireOp",EDGE,"E35.2.3")])]})]});
            var Q36;
            Q36=makeQuery(id+"F3.boolean.opBoolean","INTERSECT",EDGE,{"derivedFrom":[makeQuery(id+"F1.opRevolve","SWEPT_FACE",FACE,{"disambiguationData":[OSD([sQuery(id+"F0.wireOp",EDGE,"E12.filletArc")])]}),makeQuery(id+"F3.opExtrude","SWEPT_FACE",FACE,{"disambiguationData":[OSD([sQuery(id+"F2.wireOp",EDGE,"E35.3.0"),sQuery(id+"F2.wireOp",EDGE,"E35.3.3")])]})]});
            var Q37;
            Q37=makeQuery(id+"F3.boolean.opBoolean","INTERSECT",EDGE,{"derivedFrom":[makeQuery(id+"F1.opRevolve","SWEPT_FACE",FACE,{"disambiguationData":[OSD([sQuery(id+"F0.wireOp",EDGE,"E12.filletArc")])]}),makeQuery(id+"F3.opExtrude","SWEPT_FACE",FACE,{"disambiguationData":[OSD([sQuery(id+"F2.wireOp",EDGE,"E35.4.0"),sQuery(id+"F2.wireOp",EDGE,"E35.4.3")])]})]});
            var Q38;
            Q38=makeQuery(id+"F3.boolean.opBoolean","INTERSECT",EDGE,{"derivedFrom":[makeQuery(id+"F1.opRevolve","SWEPT_FACE",FACE,{"disambiguationData":[OSD([sQuery(id+"F0.wireOp",EDGE,"E12.filletArc")])]}),makeQuery(id+"F3.opExtrude","SWEPT_FACE",FACE,{"disambiguationData":[OSD([sQuery(id+"F2.wireOp",EDGE,"E22.trimOffspring"),sQuery(id+"F2.wireOp",EDGE,"E28.0.MirrorCS")])]})]});
            var Q39;
            Q39=makeQuery(id+"F3.boolean.opBoolean","INTERSECT",EDGE,{"derivedFrom":[makeQuery(id+"F1.opRevolve","SWEPT_FACE",FACE,{"disambiguationData":[OSD([sQuery(id+"F0.wireOp",EDGE,"E12.filletArc")])]}),makeQuery(id+"F3.opExtrude","SWEPT_FACE",FACE,{"disambiguationData":[OSD([sQuery(id+"F2.wireOp",EDGE,"E35.1.0"),sQuery(id+"F2.wireOp",EDGE,"E35.1.3")])]})]});
            fillet(context, id + "F4", {"entities" : qUnion([Q0, Q1, Q2, Q3, Q4, Q5, Q6, Q7, Q8, Q9, Q10, Q11, Q12, Q13, Q14, Q15, Q16, Q17, Q18, Q19, Q20, Q21, Q22, Q23, Q24, Q25, Q26, Q27, Q28, Q29, Q30, Q31, Q32, Q33, Q34, Q35, Q36, Q37, Q38, Q39]), "radius" : 5 * mm, "tangentPropagation" : true, "allowEdgeOverflow" : false});
        }
    });
